# Revit family: Maxlogic soket altı siren,flaşörlü siren
name_source: partatom
category: Fire Alarm Devices
units: mm (PartAtom-declared; Revit-internal decimal feet)

## family parameters
Cut with Voids When Loaded = No
Host = Face
Maintain Annotation Orientation = Yes
OmniClass Number = 23.85.30.21
OmniClass Title = Environmental Detection/Registration
Part Type = Normal
Room Calculation Point = No
Round Connector Dimension = Use Diameter
Shared = No

## types (2) — shared parameters
Color = Beyaz
Device Adress Setup = El tipi adresleme cihazı
Fax Number = (+)90 216 466 45 10
Installation Manual = https://mavilielektronik.com
Main Material = White Plastic ABS
Manufacturer = Mavili Elektronik Ticaret A.Ş.
Model = Maxlogic
Mounting surface = Tavana montaj
Nominal Depth = 32 mm
Nominal Height = 114 mm
Nominal Width = 114 mm
Operating temperature = (-10°C) - (+55°C)
Operating voltage range = 18-33V/DC
Operatonal Voltage (default) = 24 V/DC
Protection Sign = IP 21C
Secondary Material = Plastic
URL = https://www.mavili.com.tr
Warranty Duration Labor = 2
Warranty Duration Parts = 2
Warranty Duration Unit = Year
zero-valued in all types: Cost, Default Elevation

## per-type parameters (varying)
| type | Code Performance | Description | Product Code | Weight |
| Maxlogic akıllı adresli çevrimden beslemeli soket altı siren | EN 54-3 | Akıllı adresli çevrimden beslemeli soket altı siren | ML-1101 | 120 gr |
| Maxlogic akıllı adresli çevrimden beslemeli soket altı flaşörlü siren | EN 54-3 / EN 54-23 | Akıllı adresli çevrimden beslemeli soket altı flaşörlü siren | ML-1102 | 140 gr |

## geometry (parser evidence)
native form markers: Sweep x2
no freeform markers — native parametric forms only
